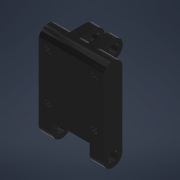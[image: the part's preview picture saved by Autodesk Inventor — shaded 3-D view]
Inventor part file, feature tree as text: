
AUTODESK INVENTOR PART (.ipt)
format: ipt  version: 2021 (Build 250183000, 183)  size: 200,704 bytes
history: native  units: mm
features: extrude x5, sketch x5, fillet x3
ambient origin geometry x8: Origin, YZ Plane, XZ Plane, XY Plane, X Axis, Y Axis, Z Axis, Center Point
bodies: Solid1 (feature_tree)
feature tree (13):
  extrude  "Extrusion1"  Depth=6.0mm
  extrude  "Extrusion2"  Depth=40.0mm
  fillet  "Fillet1"  Radius=8.2mm
  extrude  "Extrusion3"  Depth=4.1mm
  extrude  "Extrusion4"  Depth=8.2mm
  fillet  "Fillet2"  [1 undecoded]
  fillet  "Fillet3"  Radius=4.1mm
  extrude  "Extrusion5"  Depth=4.0mm
  sketch  "Sketch1"  dims[d0=6.0mm d1=6.0mm]
  sketch  "Sketch2"  dims[d2=16.0mm d3=40.0mm d4=8.2mm]
  sketch  "Sketch3"  dims[d5=8.2mm d6=0.0mm d7=4.1mm]
  sketch  "Sketch4"  dims[d8=4.1mm d9=8.2mm d10=0.0mm d11=0.0mm d12=4.1mm]
  sketch  "Sketch5"  dims[d13=4.0mm d14=4.0mm d15=4.0mm d16=2.0mm d17=8.0mm d18=8.2mm d19=0.0mm d20=4.1mm d21=8.0mm d22=4.0mm d23=4.0mm d24=0.0mm d25=0.0mm d26=4.1mm d27=4.1mm d28=20.0mm d30=20.0mm d31=20.0mm d33=20.0mm d36=1.8mm d37=10.0mm d38=2.6mm d39=10.0mm d40=0.0mm d41=28.0mm d42=23.6mm]
note: 1 required parameter value undecoded (feature->parameter linkage not recoverable at this tier; creation-order binding heuristic only, values carry confidence <= 0.55)
